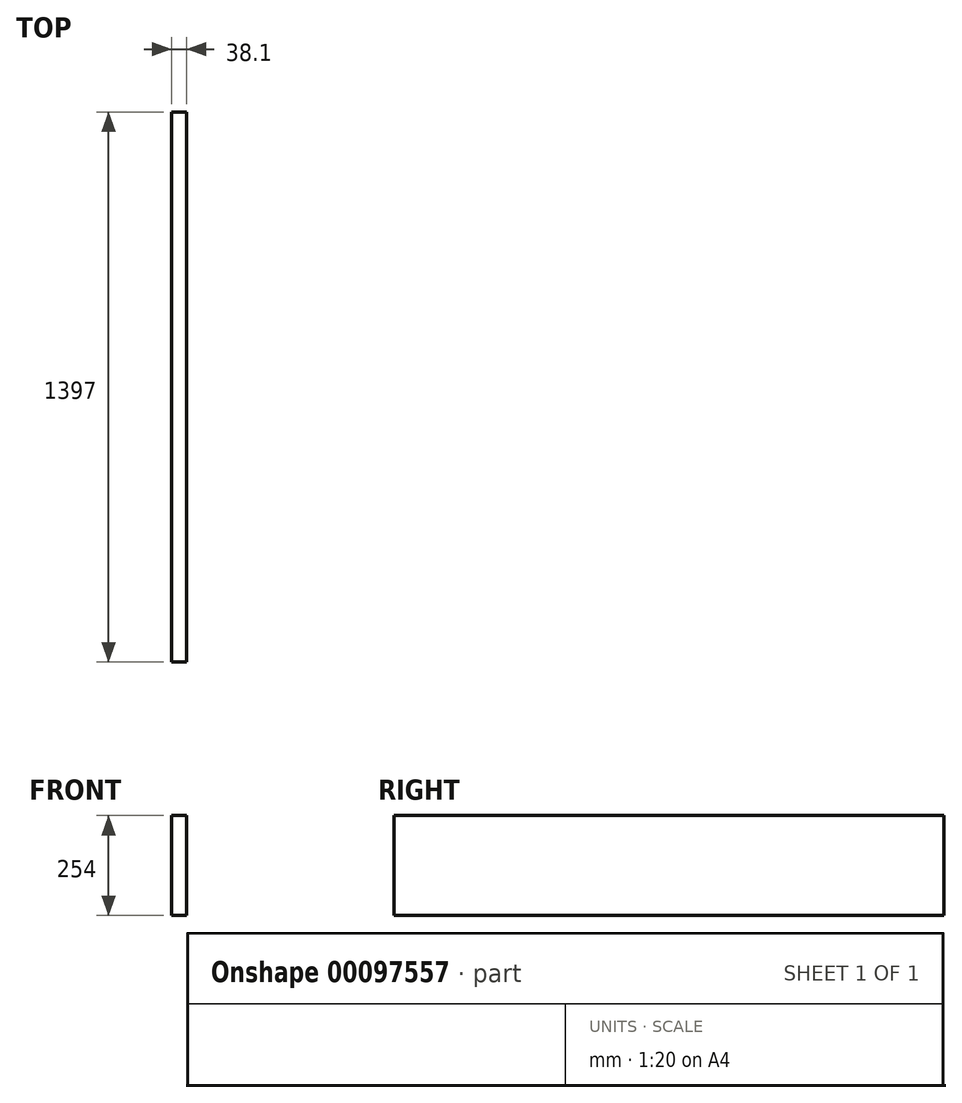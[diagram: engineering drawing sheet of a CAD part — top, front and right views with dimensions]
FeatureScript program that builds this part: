
annotation { "Feature Type Name" : "Feature", "Feature Type Description" : "" }
export const myFeature = defineFeature(function(context is Context, id is Id, definition is map)
    precondition{}
    {
        {
            var Q0;
            Q0=qCreatedBy(makeId("Right.planeOp"),FACE);
            var sketch = newSketch(context, id + "F0", { "sketchPlane" : qUnion([Q0])});
            skLineSegment(sketch, "E0.bottom", {"start": v(698.5, 127) * mm, "end": v(-698.5, 127) * mm});
            skLineSegment(sketch, "E0.top", {"start": v(698.5, -127) * mm, "end": v(-698.5, -127) * mm});
            skLineSegment(sketch, "E0.left", {"start": v(698.5, 127) * mm, "end": v(698.5, -127) * mm});
            skLineSegment(sketch, "E0.right", {"start": v(-698.5, 127) * mm, "end": v(-698.5, -127) * mm});
            skPoint(sketch, "E0.middle", {"position": v(0, 0) * mm});
            skSolve(sketch);
        }
        {
            var Q0;
            Q0=makeQuery(id+"F0.imprint","IMPRINT",FACE,{"disambiguationData":[TD([[makeQuery(id+"F0.imprint","IMPRINT",EDGE,{"derivedFrom":sQuery(id+"F0.wireOp",EDGE,"E0.bottom")}),1.0]])]});
            extrude(context, id + "F1", {"entities" : qUnion([Q0]), "depth" : 38.1 * mm});
        }
    });
